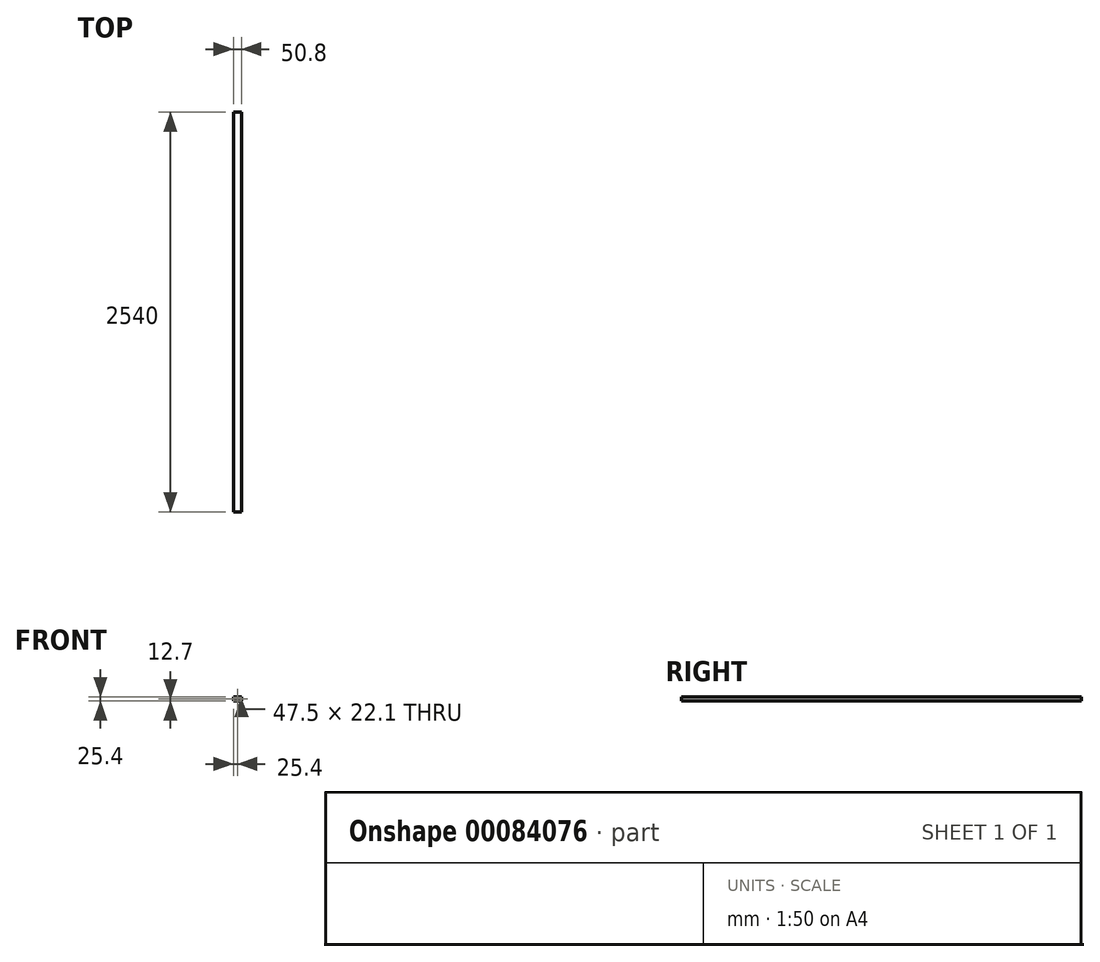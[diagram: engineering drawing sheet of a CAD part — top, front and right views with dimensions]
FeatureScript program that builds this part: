
annotation { "Feature Type Name" : "Feature", "Feature Type Description" : "" }
export const myFeature = defineFeature(function(context is Context, id is Id, definition is map)
    precondition{}
    {
        {
            var Q0;
            Q0=qCreatedBy(makeId("Front.planeOp"),FACE);
            var sketch = newSketch(context, id + "F0", { "sketchPlane" : qUnion([Q0])});
            skLineSegment(sketch, "E0.rect.bottom", {"start": v(25.4, -12.7) * mm, "end": v(-25.4, -12.7) * mm});
            skLineSegment(sketch, "E0.rect.top", {"start": v(25.4, 12.7) * mm, "end": v(-25.4, 12.7) * mm});
            skLineSegment(sketch, "E0.rect.left", {"start": v(25.4, -12.7) * mm, "end": v(25.4, 12.7) * mm});
            skLineSegment(sketch, "E0.rect.right", {"start": v(-25.4, -12.7) * mm, "end": v(-25.4, 12.7) * mm});
            skPoint(sketch, "E0.rect.middle", {"position": v(0, 0) * mm});
            skLineSegment(sketch, "E1.rect.bottom", {"start": v(23.75, -11.05) * mm, "end": v(-23.75, -11.05) * mm});
            skLineSegment(sketch, "E1.rect.top", {"start": v(23.75, 11.05) * mm, "end": v(-23.75, 11.05) * mm});
            skLineSegment(sketch, "E1.rect.left", {"start": v(23.75, -11.05) * mm, "end": v(23.75, 11.05) * mm});
            skLineSegment(sketch, "E1.rect.right", {"start": v(-23.75, -11.05) * mm, "end": v(-23.75, 11.05) * mm});
            skSolve(sketch);
        }
        {
            var Q0;
            Q0=makeQuery(id+"F0.imprint","IMPRINT",FACE,{"disambiguationData":[TD([[makeQuery(id+"F0.imprint","IMPRINT",EDGE,{"derivedFrom":sQuery(id+"F0.wireOp",EDGE,"E0.rect.bottom")}),-1.0]])]});
            extrude(context, id + "F1", {"entities" : qUnion([Q0]), "oppositeDirection" : true, "depth" : 2540 * mm});
        }
    });
